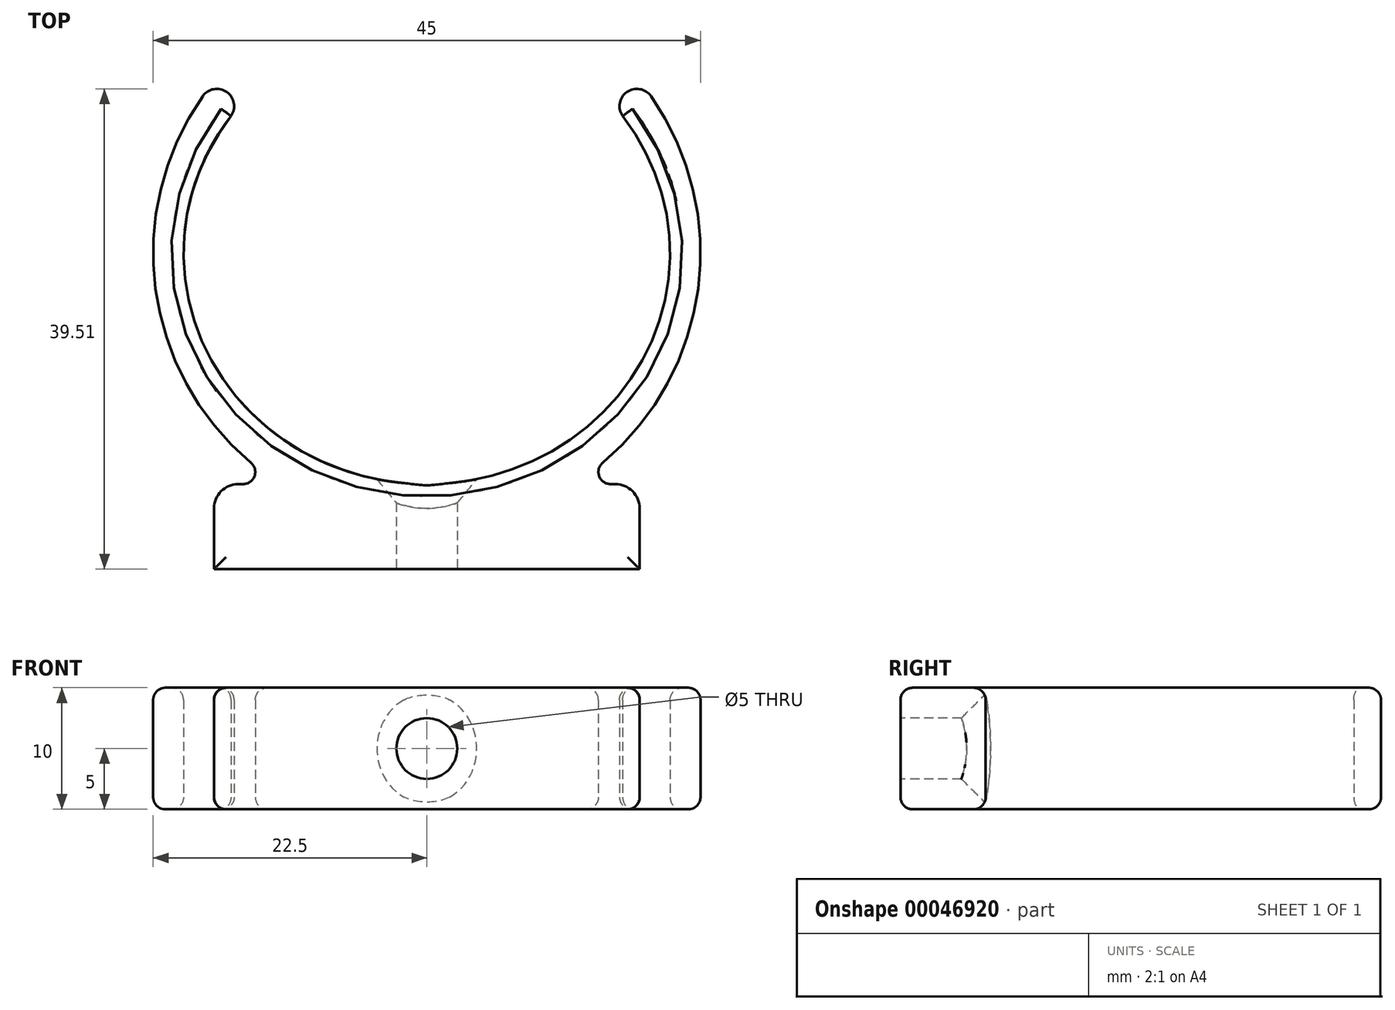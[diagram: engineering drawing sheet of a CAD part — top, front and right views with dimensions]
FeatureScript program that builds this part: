
annotation { "Feature Type Name" : "Feature", "Feature Type Description" : "" }
export const myFeature = defineFeature(function(context is Context, id is Id, definition is map)
    precondition{}
    {
        {
            var Q0;
            Q0=qCreatedBy(makeId("Top.planeOp"),FACE);
            var sketch = newSketch(context, id + "F0", { "sketchPlane" : qUnion([Q0])});
            skArc(sketch, "E0", {"start": v(-18.43, 12.9) * mm, "mid": v(-22.3, -2.94) * mm, "end": v(-14.47, -17.23) * mm});
            skEllipticalArc(sketch, "E1", {});
            skCircle(sketch, "E2", {"center": v(0, 0) * mm, "radius": 19 * mm, "construction": true});
            skLineSegment(sketch, "E3", {"start": v(0, 0) * mm, "end": v(-24.83, 17.38) * mm, "construction": true});
            skLineSegment(sketch, "E4", {"start": v(-18.43, 12.9) * mm, "end": v(-16.1, 11.27) * mm, "construction": true});
            skArc(sketch, "E5", {"start": v(-16.1, 11.27) * mm, "mid": v(-16.45, 13.25) * mm, "end": v(-18.43, 12.9) * mm});
            skArc(sketch, "E6.MirrorC", {"start": v(16.1, 11.27) * mm, "mid": v(16.45, 13.25) * mm, "end": v(18.43, 12.9) * mm});
            skLineSegment(sketch, "E7.MirrorCS", {"start": v(0, 0) * mm, "end": v(24.83, 17.38) * mm, "construction": true});
            skLineSegment(sketch, "E8.rect.bottom", {"start": v(15.5, -19) * mm, "end": v(15.1, -19) * mm});
            skLineSegment(sketch, "E8.rect.top", {"start": v(17.5, -26) * mm, "end": v(-17.5, -26) * mm});
            skLineSegment(sketch, "E8.rect.left", {"start": v(17.5, -21) * mm, "end": v(17.5, -26) * mm});
            skLineSegment(sketch, "E8.rect.right", {"start": v(-17.5, -21) * mm, "end": v(-17.5, -26) * mm});
            skPoint(sketch, "E8.rect.middle", {"position": v(0, -22.5) * mm});
            skArc(sketch, "E9.trimOffspring", {"start": v(14.47, -17.23) * mm, "mid": v(22.3, -2.94) * mm, "end": v(18.43, 12.9) * mm});
            skLineSegment(sketch, "E10.trimOffspring", {"start": v(-15.1, -19) * mm, "end": v(-15.5, -19) * mm});
            skPoint(sketch, "E11.visualSharp", {"position": v(-12.05, -19) * mm});
            skArc(sketch, "E11.filletArc", {"start": v(-15.1, -19) * mm, "mid": v(-14.17, -18.34) * mm, "end": v(-14.47, -17.23) * mm});
            skPoint(sketch, "E12.visualSharp", {"position": v(12.05, -19) * mm});
            skArc(sketch, "E12.filletArc", {"start": v(14.47, -17.23) * mm, "mid": v(14.17, -18.34) * mm, "end": v(15.1, -19) * mm});
            skPoint(sketch, "E13.visualSharp", {"position": v(-17.5, -19) * mm});
            skArc(sketch, "E13.filletArc", {"start": v(-15.5, -19) * mm, "mid": v(-16.91, -19.59) * mm, "end": v(-17.5, -21) * mm});
            skPoint(sketch, "E14.visualSharp", {"position": v(17.5, -19) * mm});
            skArc(sketch, "E14.filletArc", {"start": v(17.5, -21) * mm, "mid": v(16.91, -19.59) * mm, "end": v(15.5, -19) * mm});
            const initialGuessF0  = {"E1": [0, 0, 1, 0, 0.02, 0.019, 2.5064243449638544, 1.5707963267948966]};
            skSetInitialGuess(sketch, initialGuessF0);
            skSolve(sketch);
        }
        {
            var Q0;
            Q0=makeQuery(id+"F0.imprint","IMPRINT",FACE,{"disambiguationData":[TD([[makeQuery(id+"F0.imprint","IMPRINT",EDGE,{"derivedFrom":sQuery(id+"F0.wireOp",EDGE,"E0")}),1.0]])]});
            extrude(context, id + "F1", {"entities" : qUnion([Q0]), "depth" : 10 * mm});
        }
        {
            var Q0;
            Q0=makeQuery(id+"F1.opExtrude","SWEPT_FACE",FACE,{"disambiguationData":[OSD([sQuery(id+"F0.wireOp",EDGE,"E8.rect.top")])]});
            var sketch = newSketch(context, id + "F2", { "sketchPlane" : qUnion([Q0])});
            skLineSegment(sketch, "E15", {"start": v(0, 10) * mm, "end": v(0, 0) * mm, "construction": true});
            skCircle(sketch, "E16", {"center": v(0, 5) * mm, "radius": 2.5 * mm});
            skSolve(sketch);
        }
        {
            var Q0;
            Q0=makeQuery(id+"F2.imprint","IMPRINT",FACE,{"disambiguationData":[TD([[makeQuery(id+"F2.imprint","IMPRINT",EDGE,{"derivedFrom":sQuery(id+"F2.wireOp",EDGE,"E16")}),1.0]])]});
            extrude(context, id + "F3", {"entities" : qUnion([Q0]), "operationType" : NewBodyOperationType.REMOVE, "endBound" : BoundingType.THROUGH_ALL, "oppositeDirection" : true, "depth" : 25 * mm});
        }
        {
            var Q0;
            Q0=makeQuery(id+"F3.boolean.opBoolean","INTERSECT",EDGE,{"derivedFrom":[makeQuery(id+"F1.opExtrude","SWEPT_FACE",FACE,{"disambiguationData":[OSD([sQuery(id+"F0.wireOp",EDGE,"E1")])]}),makeQuery(id+"F3.opExtrude","SWEPT_FACE",FACE,{"disambiguationData":[OSD([sQuery(id+"F2.wireOp",EDGE,"E16")])]})]});
            chamfer(context, id + "F4", {"entities" : qUnion([Q0]), "width" : 2 * mm, "tangentPropagation" : true});
        }
        {
            var Q0;
            Q0=makeQuery(id+"F1.opExtrude","CAP_FACE",FACE,{"disambiguationData":[OSD([sQuery(id+"F0.wireOp",EDGE,"E0"),sQuery(id+"F0.wireOp",EDGE,"E1"),sQuery(id+"F0.wireOp",EDGE,"E5"),sQuery(id+"F0.wireOp",EDGE,"E6.MirrorC"),sQuery(id+"F0.wireOp",EDGE,"E8.rect.bottom"),sQuery(id+"F0.wireOp",EDGE,"E8.rect.top"),sQuery(id+"F0.wireOp",EDGE,"E8.rect.left"),sQuery(id+"F0.wireOp",EDGE,"E8.rect.right"),sQuery(id+"F0.wireOp",EDGE,"E9.trimOffspring"),sQuery(id+"F0.wireOp",EDGE,"E10.trimOffspring"),sQuery(id+"F0.wireOp",EDGE,"E11.filletArc"),sQuery(id+"F0.wireOp",EDGE,"E12.filletArc"),sQuery(id+"F0.wireOp",EDGE,"E13.filletArc"),sQuery(id+"F0.wireOp",EDGE,"E14.filletArc")])],"isStart":true});
            var Q1;
            Q1=makeQuery(id+"F1.opExtrude","CAP_FACE",FACE,{"disambiguationData":[OSD([sQuery(id+"F0.wireOp",EDGE,"E0"),sQuery(id+"F0.wireOp",EDGE,"E1"),sQuery(id+"F0.wireOp",EDGE,"E5"),sQuery(id+"F0.wireOp",EDGE,"E6.MirrorC"),sQuery(id+"F0.wireOp",EDGE,"E8.rect.bottom"),sQuery(id+"F0.wireOp",EDGE,"E8.rect.top"),sQuery(id+"F0.wireOp",EDGE,"E8.rect.left"),sQuery(id+"F0.wireOp",EDGE,"E8.rect.right"),sQuery(id+"F0.wireOp",EDGE,"E9.trimOffspring"),sQuery(id+"F0.wireOp",EDGE,"E10.trimOffspring"),sQuery(id+"F0.wireOp",EDGE,"E11.filletArc"),sQuery(id+"F0.wireOp",EDGE,"E12.filletArc"),sQuery(id+"F0.wireOp",EDGE,"E13.filletArc"),sQuery(id+"F0.wireOp",EDGE,"E14.filletArc")])],"isStart":false});
            fillet(context, id + "F5", {"entities" : qUnion([Q0, Q1]), "radius" : 1 * mm, "tangentPropagation" : true, "allowEdgeOverflow" : false});
        }
    });
